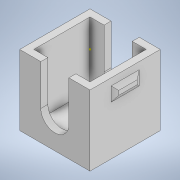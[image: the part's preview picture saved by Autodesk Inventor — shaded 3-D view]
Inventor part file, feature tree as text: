
AUTODESK INVENTOR PART (.ipt)
format: ipt  version: 2022 (Build 260153000, 153)  size: 137,728 bytes
history: native  units: in
note: dims shown in document units (in); Inventor stores cm internally (conversion verified against a paired STEP export)
features: sketch x9, extrude x4, shell x1
ambient origin geometry x8: Origin, YZ Plane, XZ Plane, XY Plane, X Axis, Y Axis, Z Axis, Center Point
bodies: Solid1 (feature_tree)
feature tree (14):
  extrude  "Extrusion1"  Depth=0.1969in
  shell  "Shell1"  Thickness=0.1969in
  extrude  "Extrusion3"  TaperAngle=0.0deg  [1 undecoded]
  sketch  "Sketch4"  dims[d10=0.0394in d11=0.0079in d12=-0.4123in]
  sketch  "Sketch5"  dims[d13=0.0394in d14=0.0787in]
  sketch  "Sketch6"  dims[d15=0.0394in]
  sketch  "Sketch7"  dims[d16=0.0787in]
  sketch  "Sketch8"  dims[d17=0.0394in]
  extrude  "Extrusion4"  Depth=0.0079in
  extrude  "Extrusion5"  Depth=0.0787in
  sketch  "Sketch1"  dims[d0=0.1969in d1=0.1969in d2=0.1969in d3=0.0in]
  sketch  "Sketch3"  dims[d4=0.0197in d8=0.0in d9=0.0in]
  sketch  "Sketch9"  dims[d18=0.0079in d19=-0.4123in]
  sketch  "Sketch10"
note: 1 required parameter value undecoded (feature->parameter linkage not recoverable at this tier; creation-order binding heuristic only, values carry confidence <= 0.55)
